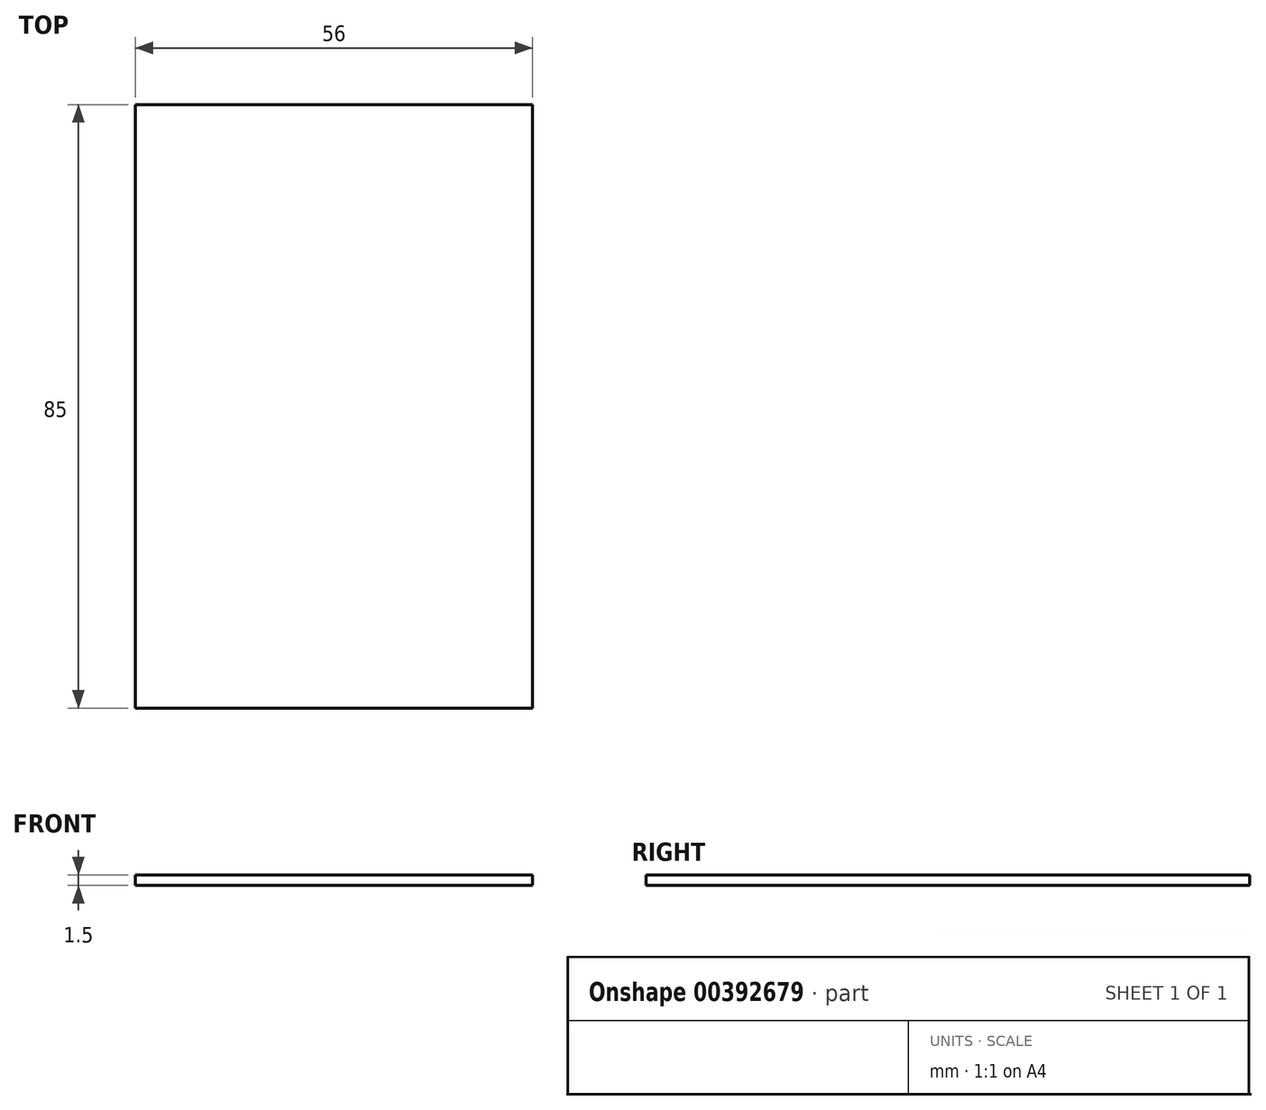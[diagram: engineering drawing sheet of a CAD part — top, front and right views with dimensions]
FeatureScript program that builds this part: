
annotation { "Feature Type Name" : "Feature", "Feature Type Description" : "" }
export const myFeature = defineFeature(function(context is Context, id is Id, definition is map)
    precondition{}
    {
        {
            var Q0;
            Q0=qCreatedBy(makeId("Top.planeOp"),FACE);
            var sketch = newSketch(context, id + "F0", { "sketchPlane" : qUnion([Q0])});
            skLineSegment(sketch, "E0.bottom", {"start": v(28, -42.5) * mm, "end": v(-28, -42.5) * mm});
            skLineSegment(sketch, "E0.top", {"start": v(28, 42.5) * mm, "end": v(-28, 42.5) * mm});
            skLineSegment(sketch, "E0.left", {"start": v(28, -42.5) * mm, "end": v(28, 42.5) * mm});
            skLineSegment(sketch, "E0.right", {"start": v(-28, -42.5) * mm, "end": v(-28, 42.5) * mm});
            skPoint(sketch, "E0.middle", {"position": v(0, 0) * mm});
            skSolve(sketch);
        }
        {
            var Q0;
            Q0 = qSketchRegion(id + "F0", true);
            extrude(context, id + "F1", {"entities" : qUnion([Q0]), "depth" : -1.5 * mm});
        }
    });
